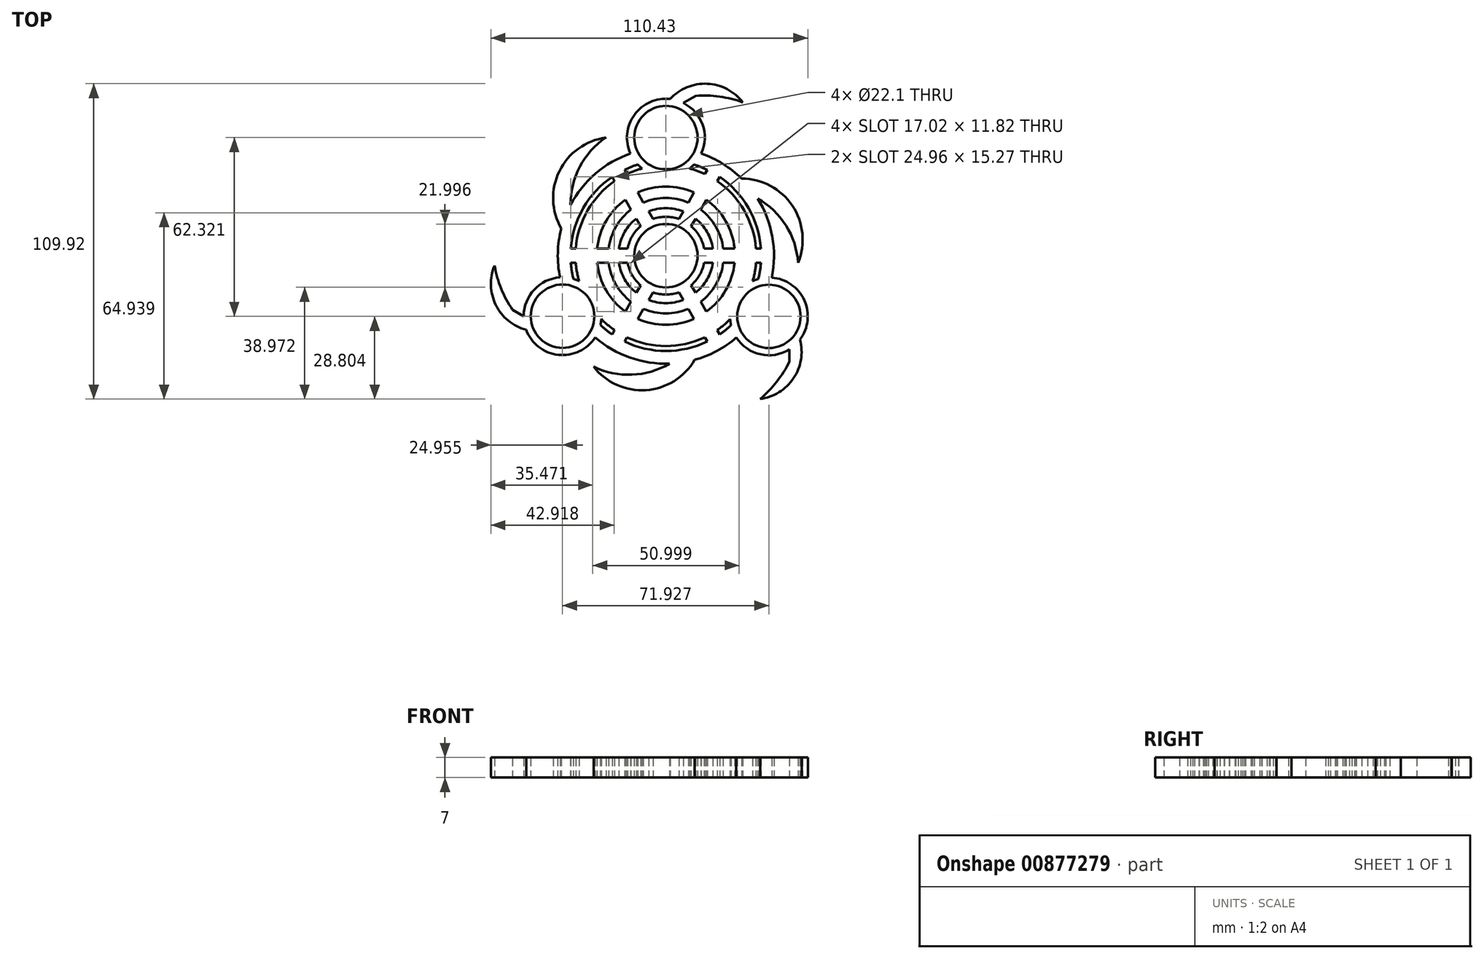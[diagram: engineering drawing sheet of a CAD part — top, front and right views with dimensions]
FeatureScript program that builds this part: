
annotation { "Feature Type Name" : "Feature", "Feature Type Description" : "" }
export const myFeature = defineFeature(function(context is Context, id is Id, definition is map)
    precondition{}
    {
        {
            var Q0;
            Q0=qCreatedBy(makeId("Top.planeOp"),FACE);
            var sketch = newSketch(context, id + "F0", { "sketchPlane" : qUnion([Q0])});
            skArc(sketch, "E0", {"start": v(13.32, 2.49) * mm, "mid": v(11.73, 6.77) * mm, "end": v(8.82, 10.3) * mm});
            skCircle(sketch, "E1", {"center": v(0, 41.15) * mm, "radius": 11.05 * mm});
            skArc(sketch, "E2", {"start": v(12.35, 35.59) * mm, "mid": v(12.78, 45.66) * mm, "end": v(6.13, 53.24) * mm});
            skArc(sketch, "E3.1.0", {"start": v(-30.25, -8.84) * mm, "mid": v(-31.22, -8.43) * mm, "end": v(-32.22, -8.1) * mm});
            skCircle(sketch, "E3.1.1", {"center": v(-36.02, -21.1) * mm, "radius": 11.05 * mm});
            skArc(sketch, "E3.2.0", {"start": v(32.22, -8.13) * mm, "mid": v(31.22, -8.45) * mm, "end": v(30.25, -8.86) * mm});
            skCircle(sketch, "E3.2.1", {"center": v(35.91, -21.17) * mm, "radius": 11.05 * mm});
            skPoint(sketch, "E3.center", {"position": v(-0.03, -0.37) * mm});
            skArc(sketch, "E4", {"start": v(-22.5, -22.07) * mm, "mid": v(-20.28, -24.13) * mm, "end": v(-17.87, -25.97) * mm});
            skArc(sketch, "E5", {"start": v(23.96, 2.49) * mm, "mid": v(20.86, 12.05) * mm, "end": v(14.14, 19.5) * mm});
            skArc(sketch, "E6", {"start": v(19.97, 2.49) * mm, "mid": v(17.43, 10.06) * mm, "end": v(12.14, 16.05) * mm});
            skArc(sketch, "E7", {"start": v(16.38, 2.49) * mm, "mid": v(14.34, 8.28) * mm, "end": v(10.34, 12.94) * mm});
            skPoint(sketch, "E8.center", {"position": v(-0.01, -0.32) * mm});
            skLineSegment(sketch, "E9", {"start": v(0, 27.6) * mm, "end": v(0, 13.55) * mm});
            skArc(sketch, "E10", {"start": v(-20.89, 41.15) * mm, "mid": v(-37.13, 29.46) * mm, "end": v(-36.47, 9.46) * mm});
            skArc(sketch, "E11", {"start": v(-20.89, 41.15) * mm, "mid": v(-30.03, 31) * mm, "end": v(-33.24, 17.73) * mm});
            skArc(sketch, "E12.1.0", {"start": v(-25.2, -38.67) * mm, "mid": v(-6.95, -46.88) * mm, "end": v(10.04, -36.31) * mm});
            skArc(sketch, "E12.1.1", {"start": v(-25.2, -38.67) * mm, "mid": v(-11.84, -41.5) * mm, "end": v(1.27, -37.65) * mm});
            skArc(sketch, "E12.2.0", {"start": v(46.08, -2.49) * mm, "mid": v(44.08, 17.42) * mm, "end": v(26.43, 26.85) * mm});
            skArc(sketch, "E12.2.1", {"start": v(46.08, -2.49) * mm, "mid": v(41.86, 10.5) * mm, "end": v(31.97, 19.93) * mm});
            skArc(sketch, "E13", {"start": v(-22.81, -24.16) * mm, "mid": v(-20.83, -25.88) * mm, "end": v(-18.72, -27.45) * mm});
            skArc(sketch, "E14", {"start": v(-24.65, -28.49) * mm, "mid": v(-12.56, -35.52) * mm, "end": v(1.27, -37.65) * mm});
            skArc(sketch, "E15.trimOffspring", {"start": v(36.89, -7.65) * mm, "mid": v(37.09, 6.61) * mm, "end": v(31.97, 19.93) * mm});
            skArc(sketch, "E16.trimOffspring", {"start": v(32.22, -8.13) * mm, "mid": v(32.8, -5.33) * mm, "end": v(33.13, -2.49) * mm});
            skArc(sketch, "E17.trimOffspring", {"start": v(-12.35, 35.59) * mm, "mid": v(-24.49, 28.63) * mm, "end": v(-33.24, 17.73) * mm});
            skArc(sketch, "E18.trimOffspring", {"start": v(-9.76, 31.76) * mm, "mid": v(-12.12, 30.94) * mm, "end": v(-14.41, 29.94) * mm});
            skLineSegment(sketch, "E19", {"start": v(-53.6, -13.53) * mm, "end": v(-54.1, -13.26) * mm});
            skArc(sketch, "E20.trimOffspring", {"start": v(30.25, -8.86) * mm, "mid": v(31, -5.7) * mm, "end": v(31.42, -2.49) * mm});
            skArc(sketch, "E21.trimOffspring", {"start": v(-8.26, 30.42) * mm, "mid": v(-10.95, 29.55) * mm, "end": v(-13.56, 28.46) * mm});
            skArc(sketch, "E22", {"start": v(-59.7, -3.47) * mm, "mid": v(-59.28, -17.16) * mm, "end": v(-48.7, -25.87) * mm});
            skArc(sketch, "E23", {"start": v(-59.7, -3.47) * mm, "mid": v(-57.39, -11.5) * mm, "end": v(-53.45, -18.88) * mm});
            skArc(sketch, "E24.1.0", {"start": v(32.86, -49.97) * mm, "mid": v(38.66, -43.95) * mm, "end": v(43.07, -36.85) * mm});
            skArc(sketch, "E24.1.1", {"start": v(32.86, -49.97) * mm, "mid": v(44.49, -42.77) * mm, "end": v(46.76, -29.28) * mm});
            skArc(sketch, "E24.2.0", {"start": v(26.84, 53.44) * mm, "mid": v(18.73, 55.45) * mm, "end": v(10.38, 55.73) * mm});
            skArc(sketch, "E24.2.1", {"start": v(26.84, 53.44) * mm, "mid": v(14.44, 59.93) * mm, "end": v(1.48, 54.62) * mm});
            skLineSegment(sketch, "E25", {"start": v(-49.57, -21.09) * mm, "end": v(-53.45, -18.88) * mm});
            skLineSegment(sketch, "E26.1.0", {"start": v(43.07, -36.85) * mm, "end": v(43.05, -32.68) * mm});
            skLineSegment(sketch, "E26.2.0", {"start": v(10.38, 55.73) * mm, "end": v(6.13, 53.24) * mm});
            skLineSegment(sketch, "E27.bottom", {"start": v(-33.13, -2.49) * mm, "end": v(-31.42, -2.49) * mm});
            skLineSegment(sketch, "E27.top", {"start": v(-33.13, 2.49) * mm, "end": v(-31.42, 2.49) * mm});
            skLineSegment(sketch, "E28.1.0", {"start": v(14.41, -29.94) * mm, "end": v(13.56, -28.46) * mm});
            skLineSegment(sketch, "E28.1.2", {"start": v(18.72, -27.45) * mm, "end": v(17.87, -25.97) * mm});
            skLineSegment(sketch, "E28.2.0", {"start": v(18.72, 27.45) * mm, "end": v(17.87, 25.97) * mm});
            skLineSegment(sketch, "E28.2.2", {"start": v(14.41, 29.94) * mm, "end": v(13.56, 28.46) * mm});
            skLineSegment(sketch, "E29.trimOffspring", {"start": v(-4.5, 12.78) * mm, "end": v(-6.03, 15.43) * mm});
            skLineSegment(sketch, "E30.trimOffspring", {"start": v(-8.82, 10.3) * mm, "end": v(-10.34, 12.94) * mm});
            skLineSegment(sketch, "E31.trimOffspring", {"start": v(-8.82, -10.3) * mm, "end": v(-10.34, -12.94) * mm});
            skLineSegment(sketch, "E32.trimOffspring", {"start": v(-4.5, -12.78) * mm, "end": v(-6.03, -15.43) * mm});
            skLineSegment(sketch, "E33.trimOffspring", {"start": v(13.32, -2.49) * mm, "end": v(16.38, -2.49) * mm});
            skLineSegment(sketch, "E34.trimOffspring", {"start": v(13.32, 2.49) * mm, "end": v(16.38, 2.49) * mm});
            skPoint(sketch, "E35.orphan", {"position": v(34.33, 2.49) * mm});
            skPoint(sketch, "E36.orphan", {"position": v(34.33, -2.49) * mm});
            skArc(sketch, "E37.trimOffspring", {"start": v(33.13, 2.49) * mm, "mid": v(28.77, 16.61) * mm, "end": v(18.72, 27.45) * mm});
            skArc(sketch, "E38.trimOffspring", {"start": v(31.42, 2.49) * mm, "mid": v(27.3, 15.76) * mm, "end": v(17.87, 25.97) * mm});
            skLineSegment(sketch, "E39.trimOffspring", {"start": v(31.42, 2.49) * mm, "end": v(33.13, 2.49) * mm});
            skLineSegment(sketch, "E40.trimOffspring", {"start": v(31.42, -2.49) * mm, "end": v(33.13, -2.49) * mm});
            skLineSegment(sketch, "E41.trimOffspring", {"start": v(19.97, 2.49) * mm, "end": v(23.96, 2.49) * mm});
            skLineSegment(sketch, "E42.trimOffspring", {"start": v(19.97, -2.49) * mm, "end": v(23.96, -2.49) * mm});
            skLineSegment(sketch, "E43.trimOffspring", {"start": v(-16.38, -2.49) * mm, "end": v(-13.32, -2.49) * mm});
            skLineSegment(sketch, "E44.trimOffspring", {"start": v(-16.38, 2.49) * mm, "end": v(-13.32, 2.49) * mm});
            skArc(sketch, "E45.trimOffspring", {"start": v(-16.38, -2.49) * mm, "mid": v(-14.34, -8.28) * mm, "end": v(-10.34, -12.94) * mm});
            skArc(sketch, "E46.trimOffspring", {"start": v(-13.32, -2.49) * mm, "mid": v(-11.73, -6.77) * mm, "end": v(-8.82, -10.3) * mm});
            skArc(sketch, "E47.trimOffspring", {"start": v(-23.96, -2.49) * mm, "mid": v(-20.86, -12.05) * mm, "end": v(-14.14, -19.5) * mm});
            skArc(sketch, "E48.trimOffspring", {"start": v(-19.97, -2.49) * mm, "mid": v(-17.43, -10.06) * mm, "end": v(-12.14, -16.05) * mm});
            skLineSegment(sketch, "E49.trimOffspring", {"start": v(-23.96, 2.49) * mm, "end": v(-19.97, 2.49) * mm});
            skLineSegment(sketch, "E50.trimOffspring", {"start": v(-23.96, -2.49) * mm, "end": v(-19.97, -2.49) * mm});
            skPoint(sketch, "E51.orphan", {"position": v(-27.45, 1.01) * mm});
            skArc(sketch, "E52.trimOffspring", {"start": v(-31.42, -2.49) * mm, "mid": v(-31, -5.7) * mm, "end": v(-30.25, -8.84) * mm});
            skArc(sketch, "E53.trimOffspring", {"start": v(-33.13, -2.49) * mm, "mid": v(-32.8, -5.31) * mm, "end": v(-32.22, -8.1) * mm});
            skPoint(sketch, "E27.left.end.orphan", {"position": v(-34.33, 2.49) * mm});
            skPoint(sketch, "E27.left.start.orphan", {"position": v(-34.33, -2.49) * mm});
            skArc(sketch, "E54.trimOffspring", {"start": v(8.82, -10.3) * mm, "mid": v(11.73, -6.78) * mm, "end": v(13.32, -2.49) * mm});
            skArc(sketch, "E55.trimOffspring", {"start": v(10.34, -12.94) * mm, "mid": v(14.34, -8.28) * mm, "end": v(16.38, -2.49) * mm});
            skArc(sketch, "E56.trimOffspring", {"start": v(12.14, -16.05) * mm, "mid": v(17.43, -10.06) * mm, "end": v(19.97, -2.49) * mm});
            skArc(sketch, "E57.trimOffspring", {"start": v(14.14, -19.5) * mm, "mid": v(20.86, -12.05) * mm, "end": v(23.96, -2.49) * mm});
            skArc(sketch, "E58.trimOffspring", {"start": v(18.72, -27.45) * mm, "mid": v(20.78, -25.93) * mm, "end": v(22.72, -24.25) * mm});
            skArc(sketch, "E59.trimOffspring", {"start": v(17.87, -25.97) * mm, "mid": v(20.22, -24.18) * mm, "end": v(22.4, -22.18) * mm});
            skLineSegment(sketch, "E60.trimOffspring", {"start": v(9.83, -22) * mm, "end": v(7.83, -18.54) * mm});
            skLineSegment(sketch, "E61.trimOffspring", {"start": v(14.14, -19.5) * mm, "end": v(12.14, -16.05) * mm});
            skLineSegment(sketch, "E62.trimOffspring", {"start": v(6.03, -15.43) * mm, "end": v(4.5, -12.78) * mm});
            skLineSegment(sketch, "E63.trimOffspring", {"start": v(10.34, -12.94) * mm, "end": v(8.82, -10.3) * mm});
            skArc(sketch, "E64.trimOffspring", {"start": v(-4.5, -12.78) * mm, "mid": v(0, -13.55) * mm, "end": v(4.5, -12.78) * mm});
            skArc(sketch, "E65.trimOffspring", {"start": v(-6.03, -15.43) * mm, "mid": v(0, -16.56) * mm, "end": v(6.03, -15.43) * mm});
            skArc(sketch, "E66.trimOffspring", {"start": v(-7.83, -18.54) * mm, "mid": v(0, -20.13) * mm, "end": v(7.83, -18.54) * mm});
            skArc(sketch, "E67.trimOffspring", {"start": v(-9.83, -22) * mm, "mid": v(0, -24.1) * mm, "end": v(9.83, -22) * mm});
            skArc(sketch, "E68.trimOffspring", {"start": v(-13.56, -28.46) * mm, "mid": v(0, -31.52) * mm, "end": v(13.56, -28.46) * mm});
            skArc(sketch, "E69.trimOffspring", {"start": v(-14.41, -29.94) * mm, "mid": v(0, -33.23) * mm, "end": v(14.41, -29.94) * mm});
            skPoint(sketch, "E70.orphan", {"position": v(-19.32, -28.49) * mm});
            skPoint(sketch, "E71.orphan", {"position": v(-15.01, -30.98) * mm});
            skPoint(sketch, "E72.orphan", {"position": v(15.01, -30.98) * mm});
            skPoint(sketch, "E73.orphan", {"position": v(19.32, -28.49) * mm});
            skLineSegment(sketch, "E74.trimOffspring", {"start": v(-13.56, -28.46) * mm, "end": v(-14.41, -29.94) * mm});
            skLineSegment(sketch, "E75.trimOffspring", {"start": v(-17.87, -25.97) * mm, "end": v(-18.72, -27.45) * mm});
            skLineSegment(sketch, "E76.trimOffspring", {"start": v(-12.14, -16.05) * mm, "end": v(-14.14, -19.5) * mm});
            skLineSegment(sketch, "E77.trimOffspring", {"start": v(-7.83, -18.54) * mm, "end": v(-9.83, -22) * mm});
            skArc(sketch, "E78.trimOffspring", {"start": v(-8.82, 10.3) * mm, "mid": v(-11.73, 6.77) * mm, "end": v(-13.32, 2.49) * mm});
            skArc(sketch, "E79.trimOffspring", {"start": v(-10.34, 12.94) * mm, "mid": v(-14.34, 8.28) * mm, "end": v(-16.38, 2.49) * mm});
            skArc(sketch, "E80.trimOffspring", {"start": v(-12.14, 16.05) * mm, "mid": v(-17.43, 10.06) * mm, "end": v(-19.97, 2.49) * mm});
            skArc(sketch, "E81.trimOffspring", {"start": v(-14.14, 19.5) * mm, "mid": v(-20.86, 12.05) * mm, "end": v(-23.96, 2.49) * mm});
            skArc(sketch, "E82.trimOffspring", {"start": v(-17.87, 25.97) * mm, "mid": v(-27.3, 15.76) * mm, "end": v(-31.42, 2.49) * mm});
            skArc(sketch, "E83.trimOffspring", {"start": v(-18.72, 27.45) * mm, "mid": v(-28.77, 16.61) * mm, "end": v(-33.13, 2.49) * mm});
            skArc(sketch, "E84.trimOffspring", {"start": v(4.5, 12.78) * mm, "mid": v(0, 13.55) * mm, "end": v(-4.5, 12.78) * mm});
            skPoint(sketch, "E85.orphan", {"position": v(-15.01, 30.98) * mm});
            skPoint(sketch, "E86.orphan", {"position": v(-19.32, 28.49) * mm});
            skArc(sketch, "E87.trimOffspring", {"start": v(6.03, 15.43) * mm, "mid": v(0, 16.56) * mm, "end": v(-6.03, 15.43) * mm});
            skArc(sketch, "E88.trimOffspring", {"start": v(7.83, 18.54) * mm, "mid": v(0, 20.13) * mm, "end": v(-7.83, 18.54) * mm});
            skArc(sketch, "E89.trimOffspring", {"start": v(9.83, 22) * mm, "mid": v(0, 24.1) * mm, "end": v(-9.83, 22) * mm});
            skArc(sketch, "E90.trimOffspring", {"start": v(13.56, 28.46) * mm, "mid": v(10.95, 29.55) * mm, "end": v(8.26, 30.42) * mm});
            skArc(sketch, "E91.trimOffspring", {"start": v(14.41, 29.94) * mm, "mid": v(12.12, 30.94) * mm, "end": v(9.76, 31.76) * mm});
            skPoint(sketch, "E92.orphan", {"position": v(15.01, 30.98) * mm});
            skPoint(sketch, "E93.orphan", {"position": v(19.32, 28.49) * mm});
            skLineSegment(sketch, "E94.trimOffspring", {"start": v(9.83, 22) * mm, "end": v(7.83, 18.54) * mm});
            skLineSegment(sketch, "E95.trimOffspring", {"start": v(14.14, 19.5) * mm, "end": v(12.14, 16.05) * mm});
            skLineSegment(sketch, "E96.trimOffspring", {"start": v(-13.56, 28.46) * mm, "end": v(-14.41, 29.94) * mm});
            skLineSegment(sketch, "E97.trimOffspring", {"start": v(-17.87, 25.97) * mm, "end": v(-18.72, 27.45) * mm});
            skLineSegment(sketch, "E98.trimOffspring", {"start": v(6.03, 15.43) * mm, "end": v(4.5, 12.78) * mm});
            skLineSegment(sketch, "E99.trimOffspring", {"start": v(-7.83, 18.54) * mm, "end": v(-9.83, 22) * mm});
            skLineSegment(sketch, "E100.trimOffspring", {"start": v(-12.14, 16.05) * mm, "end": v(-14.14, 19.5) * mm});
            skLineSegment(sketch, "E101.trimOffspring", {"start": v(10.34, 12.94) * mm, "end": v(8.82, 10.3) * mm});
            skArc(sketch, "E102.trimOffspring", {"start": v(8.26, 30.42) * mm, "mid": v(9.04, 31.06) * mm, "end": v(9.76, 31.76) * mm});
            skArc(sketch, "E103.trimOffspring", {"start": v(-9.76, 31.76) * mm, "mid": v(-9.04, 31.06) * mm, "end": v(-8.26, 30.42) * mm});
            skPoint(sketch, "E104.orphan", {"position": v(4.82, 52.48) * mm});
            skArc(sketch, "E105.trimOffspring", {"start": v(1.48, 54.62) * mm, "mid": v(-10.96, 49.12) * mm, "end": v(-12.35, 35.59) * mm});
            skCircle(sketch, "E106", {"center": v(0, 0) * mm, "radius": 11.05 * mm});
            skArc(sketch, "E107.trimOffspring", {"start": v(24.56, -28.57) * mm, "mid": v(32.97, -34.4) * mm, "end": v(43.05, -32.68) * mm});
            skPoint(sketch, "E108.orphan", {"position": v(43.04, -30.42) * mm});
            skPoint(sketch, "E109.orphan", {"position": v(46.22, -27.6) * mm});
            skArc(sketch, "E110.trimOffspring", {"start": v(46.76, -29.28) * mm, "mid": v(48.24, -15.54) * mm, "end": v(36.89, -7.65) * mm});
            skArc(sketch, "E111.trimOffspring", {"start": v(10.04, -36.31) * mm, "mid": v(17.73, -33.24) * mm, "end": v(24.56, -28.57) * mm});
            skArc(sketch, "E112.trimOffspring", {"start": v(-22.81, -24.16) * mm, "mid": v(-22.62, -23.12) * mm, "end": v(-22.5, -22.07) * mm});
            skArc(sketch, "E113.trimOffspring", {"start": v(-36.9, -7.59) * mm, "mid": v(-45.9, -11.84) * mm, "end": v(-49.57, -21.09) * mm});
            skArc(sketch, "E114.trimOffspring", {"start": v(-48.7, -25.87) * mm, "mid": v(-37.48, -34.58) * mm, "end": v(-24.65, -28.49) * mm});
            skPoint(sketch, "E115.orphan", {"position": v(-47.01, -26.23) * mm});
            skArc(sketch, "E116.trimOffspring", {"start": v(-36.47, 9.46) * mm, "mid": v(-37.66, 0.96) * mm, "end": v(-36.9, -7.59) * mm});
            skPoint(sketch, "E117.orphan", {"position": v(0.8, 53.83) * mm});
            skArc(sketch, "E118.trimOffspring", {"start": v(26.43, 26.85) * mm, "mid": v(19.88, 32) * mm, "end": v(12.35, 35.59) * mm});
            skArc(sketch, "E119.trimOffspring", {"start": v(22.4, -22.18) * mm, "mid": v(22.52, -23.22) * mm, "end": v(22.72, -24.25) * mm});
            skSolve(sketch);
        }
        {
            var Q0;
            Q0=makeQuery(id+"F0.imprint","IMPRINT",FACE,{"disambiguationData":[TD([[makeQuery(id+"F0.imprint","IMPRINT",EDGE,{"derivedFrom":sQuery(id+"F0.wireOp",EDGE,"E0")}),1.0]])]});
            extrude(context, id + "F1", {"entities" : qUnion([Q0]), "depth" : 7 * mm, "offsetDistance" : 25 * mm});
        }
    });
